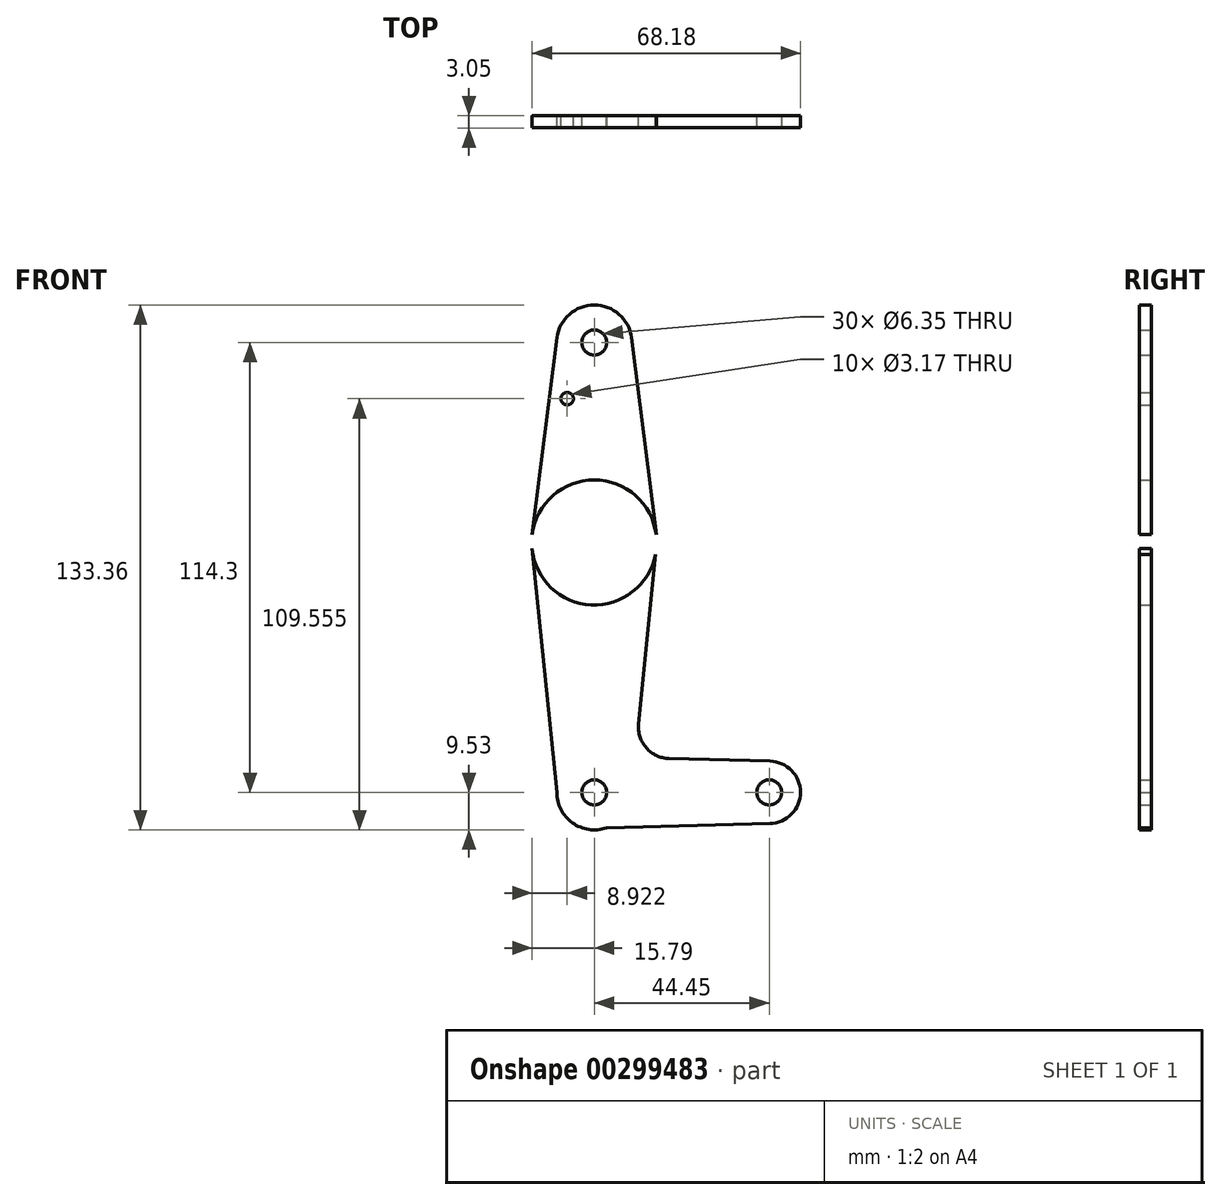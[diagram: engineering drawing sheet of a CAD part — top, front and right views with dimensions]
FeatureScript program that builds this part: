
annotation { "Feature Type Name" : "Feature", "Feature Type Description" : "" }
export const myFeature = defineFeature(function(context is Context, id is Id, definition is map)
    precondition{}
    {
        {
            var Q0;
            Q0=qCreatedBy(makeId("Front.planeOp"),FACE);
            var sketch = newSketch(context, id + "F0", { "sketchPlane" : qUnion([Q0])});
            skCircle(sketch, "E0", {"center": v(0, 0) * mm, "radius": 9.53 * mm});
            skLineSegment(sketch, "E1", {"start": v(0, 114.3) * mm, "end": v(0, 0) * mm});
            skCircle(sketch, "E2", {"center": v(0, 114.3) * mm, "radius": 9.53 * mm});
            skCircle(sketch, "E3", {"center": v(0, 63.5) * mm, "radius": 15.88 * mm});
            skLineSegment(sketch, "E4", {"start": v(0, 0) * mm, "end": v(44.45, 0) * mm});
            skCircle(sketch, "E5", {"center": v(44.45, 0) * mm, "radius": 7.94 * mm});
            skLineSegment(sketch, "E6", {"start": v(-15.75, 65.48) * mm, "end": v(-9.45, 115.5) * mm});
            skLineSegment(sketch, "E7", {"start": v(15.75, 65.48) * mm, "end": v(9.45, 115.5) * mm});
            skLineSegment(sketch, "E8", {"start": v(15.87, 63.5) * mm, "end": v(11.3, 17.34) * mm});
            skLineSegment(sketch, "E9", {"start": v(19, 8.6) * mm, "end": v(44.66, 7.93) * mm});
            skLineSegment(sketch, "E10", {"start": v(44.66, -7.93) * mm, "end": v(0, -9.1) * mm});
            skCircle(sketch, "E11", {"center": v(0, 114.3) * mm, "radius": 3.18 * mm});
            skCircle(sketch, "E12", {"center": v(0, 63.5) * mm, "radius": 3.18 * mm});
            skCircle(sketch, "E13", {"center": v(0, 0) * mm, "radius": 3.18 * mm});
            skCircle(sketch, "E14", {"center": v(44.45, 0) * mm, "radius": 3.18 * mm});
            skCircle(sketch, "E15", {"center": v(-6.87, 100.03) * mm, "radius": 1.59 * mm});
            skPoint(sketch, "E16.newPointA", {"position": v(9.57, 0) * mm});
            skArc(sketch, "E16.filletArc", {"start": v(11.3, 17.34) * mm, "mid": v(13.24, 11.3) * mm, "end": v(19, 8.6) * mm});
            skLineSegment(sketch, "E17", {"start": v(-9.52, 0) * mm, "end": v(-15.8, 61.9) * mm});
            skSolve(sketch);
        }
        {
            var Q0;
            {var subQ0=sQuery(id+"F0.wireOp",EDGE,"E17");Q0=makeQuery(id+"F0.imprint","IMPRINT",FACE,{"disambiguationData":[TD([[makeQuery(id+"F0.imprint","IMPRINT",EDGE,{"derivedFrom":subQ0}),-1.0]])]});}
            var Q1;
            {var subQ12=sQuery(id+"F0.wireOp",EDGE,"E9");Q1=makeQuery(id+"F0.imprint","IMPRINT",FACE,{"disambiguationData":[TD([[makeQuery(id+"F0.imprint","IMPRINT",EDGE,{"derivedFrom":subQ12}),-1.0]])]});}
            var Q2;
            {var subQ0=sQuery(id+"F0.wireOp",EDGE,"E3");var subQ5=sQuery(id+"F0.wireOp",EDGE,"E1");var subQ10=makeQuery(id+"F0.imprint","INTERSECT",VERTEX,{"disambiguationData":[OD(0.0)],"derivedFrom":[subQ5,subQ0]});Q2=makeQuery(id+"F0.imprint","IMPRINT",FACE,{"disambiguationData":[TD([[makeQuery(id+"F0.imprint","IMPRINT",EDGE,{"disambiguationData":[TD([[subQ10,-1.0]])],"derivedFrom":subQ5}),1.0]])]});}
            var Q3;
            {var subQ0=sQuery(id+"F0.wireOp",EDGE,"E3");var subQ2=sQuery(id+"F0.wireOp",EDGE,"E1");var subQ3=makeQuery(id+"F0.imprint","INTERSECT",VERTEX,{"disambiguationData":[OD(0.0)],"derivedFrom":[subQ2,subQ0]});Q3=makeQuery(id+"F0.imprint","IMPRINT",FACE,{"disambiguationData":[TD([[makeQuery(id+"F0.imprint","IMPRINT",EDGE,{"disambiguationData":[TD([[subQ3,-1.0]])],"derivedFrom":subQ2}),-1.0]])]});}
            var Q4;
            {var subQ5=sQuery(id+"F0.wireOp",EDGE,"E7");Q4=makeQuery(id+"F0.imprint","IMPRINT",FACE,{"disambiguationData":[TD([[makeQuery(id+"F0.imprint","IMPRINT",EDGE,{"derivedFrom":subQ5}),1.0]])]});}
            var Q5;
            {var subQ0=sQuery(id+"F0.wireOp",EDGE,"E6");Q5=makeQuery(id+"F0.imprint","IMPRINT",FACE,{"disambiguationData":[TD([[makeQuery(id+"F0.imprint","IMPRINT",EDGE,{"derivedFrom":subQ0}),-1.0]])]});}
            var Q6;
            Q6=makeQuery(id+"F0.imprint","IMPRINT",FACE,{"disambiguationData":[TD([[makeQuery(id+"F0.imprint","IMPRINT",EDGE,{"derivedFrom":sQuery(id+"F0.wireOp",EDGE,"E11")}),-1.0]])]});
            var Q7;
            {var subQ1=sQuery(id+"F0.wireOp",EDGE,"E0");var subQ10=makeQuery(id+"F0.imprint","INTERSECT",VERTEX,{"derivedFrom":[subQ1,sQuery(id+"F0.wireOp",EDGE,"E17")]});Q7=makeQuery(id+"F0.imprint","IMPRINT",FACE,{"disambiguationData":[TD([[makeQuery(id+"F0.imprint","IMPRINT",EDGE,{"disambiguationData":[TD([[subQ10,1.0]])],"derivedFrom":subQ1}),1.0]])]});}
            var Q8;
            {var subQ0=sQuery(id+"F0.wireOp",EDGE,"E1");var subQ1=sQuery(id+"F0.wireOp",EDGE,"E0");var subQ2=makeQuery(id+"F0.imprint","INTERSECT",VERTEX,{"derivedFrom":[subQ1,subQ0]});Q8=makeQuery(id+"F0.imprint","IMPRINT",FACE,{"disambiguationData":[TD([[makeQuery(id+"F0.imprint","IMPRINT",EDGE,{"disambiguationData":[TD([[subQ2,1.0]])],"derivedFrom":subQ1}),1.0]])]});}
            var Q9;
            {var subQ0=sQuery(id+"F0.wireOp",EDGE,"E10");var subQ1=sQuery(id+"F0.wireOp",EDGE,"E0");var subQ2=makeQuery(id+"F0.imprint","INTERSECT",VERTEX,{"disambiguationData":[OD(1.0)],"derivedFrom":[subQ1,subQ0]});Q9=makeQuery(id+"F0.imprint","IMPRINT",FACE,{"disambiguationData":[TD([[makeQuery(id+"F0.imprint","IMPRINT",EDGE,{"disambiguationData":[TD([[subQ2,-1.0]])],"derivedFrom":subQ1}),-1.0]])]});}
            var Q10;
            Q10=makeQuery(id+"F0.imprint","IMPRINT",FACE,{"disambiguationData":[TD([[makeQuery(id+"F0.imprint","IMPRINT",EDGE,{"derivedFrom":sQuery(id+"F0.wireOp",EDGE,"E14")}),-1.0]])]});
            extrude(context, id + "F1", {"entities" : qUnion([Q0, Q1, Q2, Q3, Q4, Q5, Q6, Q7, Q8, Q9, Q10]), "depth" : 3.05 * mm});
        }
    });
